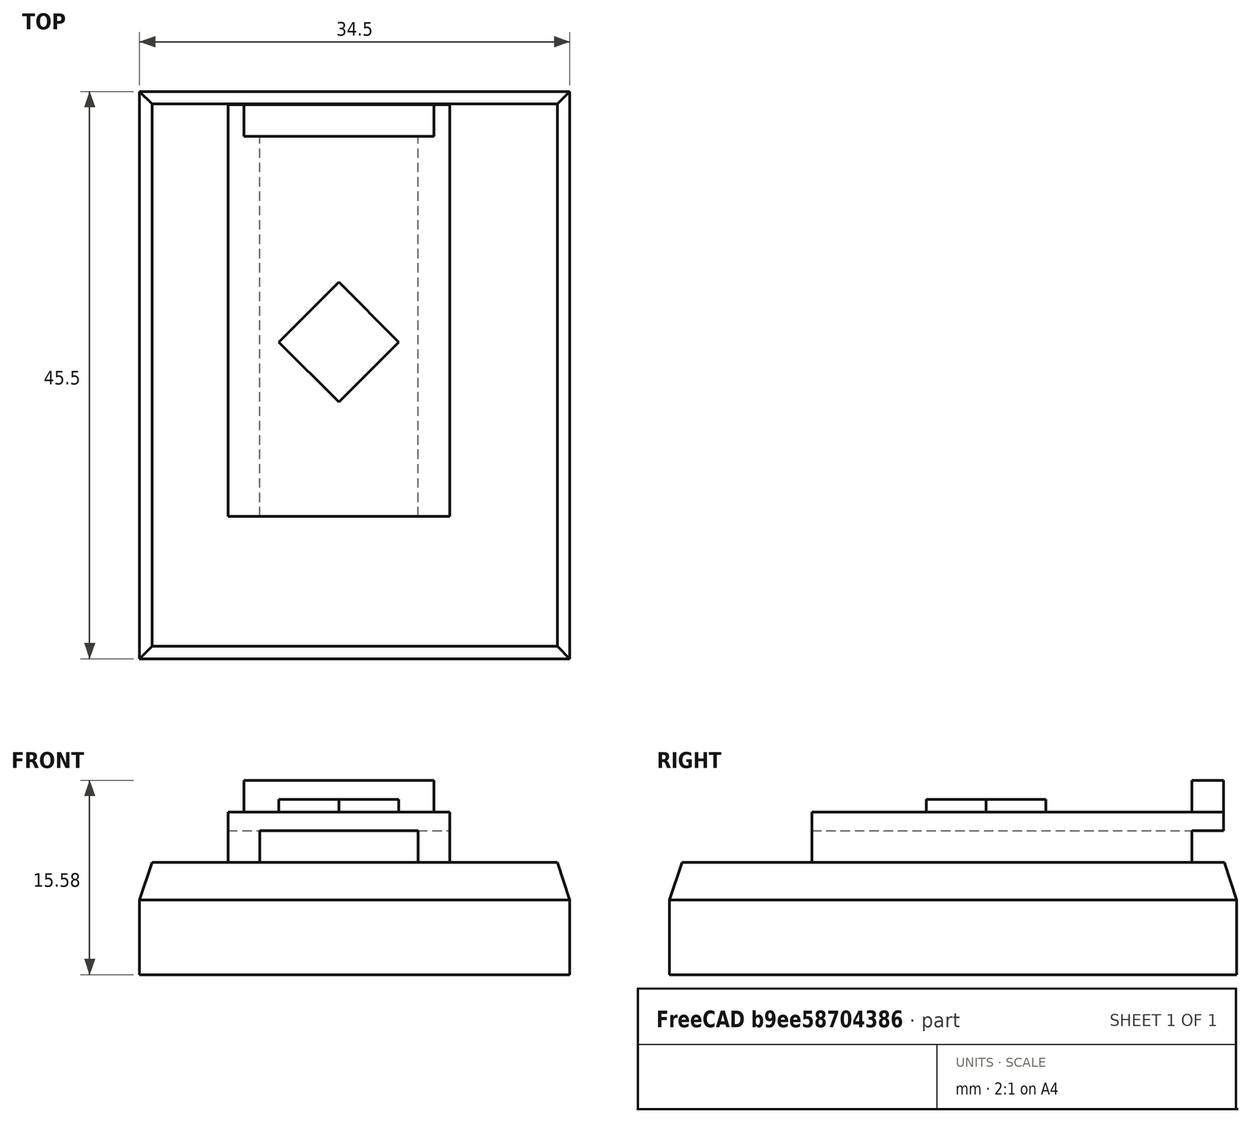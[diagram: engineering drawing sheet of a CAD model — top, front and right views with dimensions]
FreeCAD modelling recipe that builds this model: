
FCSTD DOCUMENT  (FreeCAD 0.14R3692 (Git))
Label: arduino-breadboard
License: The MIT License
LicenseURL: http://opensource.org/licenses/MIT
objects: Part::Box×5, Part::MultiFuse×2, Part::Chamfer×1, Part::Feature×1
note: 9 computed .brp shape members not serialized (recipe doc carries the construction recipe); baked Part::Feature solids carry a one-line shape summary decoded from their .brp

FEATURE [Part::Box] Box  label="breadboard"
  Height = 9
  Length = 34.5
  Width = 45.5
FEATURE [Part::Chamfer] Chamfer  label="breadboard-chamfer"
  Base = -> Box
  Edges = 4 edges: [Edge2 r1=3 r2=1,Edge6 r1=3 r2=1,Edge10 r1=3 r2=1,Edge12 r1=3 r2=1]
FEATURE [Part::Feature] Box003001  label="pin-header-left"
  Placement = pos=(15.24,0,-2.54) rot=(0,0,1;0rad)
  shape: bbox 2.54 x 30.48 x 2.54 mm, 6 faces (baked)
FEATURE [Part::Box] Box002  label="atmega-328"
  Height = 1
  Length = 6.8
  Placement = pos=(8.89,9.16167,1.5) rot=(0,0,1;0.785398rad)
  Width = 6.8
FEATURE [Part::Box] Box003  label="pin-header-right"
  Height = 2.54
  Length = 2.54
  Placement = pos=(0,0,-2.54) rot=(0,0,1;0rad)
  Width = 30.48
FEATURE [Part::Box] Box003002  label="pin-header-rear"
  Height = 2.54
  Length = 15.24
  Placement = pos=(1.27,30.48,1.5) rot=(0,0,1;0rad)
  Width = 2.54
FEATURE [Part::Box] Box001  label="pcb"
  Height = 1.5
  Length = 17.78
  Width = 33.02
FEATURE [Part::MultiFuse] Fusion  label="arduino-board"
  Placement = pos=(7.09,11.43,11.54) rot=(0,0,1;0rad)
  Shapes = -> [Box001,Box003001,Box003002,Box002,Box003]
FEATURE [Part::MultiFuse] Fusion001  label="arduino-breadboard"
  Placement = pos=(-17.25,0,0) rot=(0,0,1;0rad)
  Shapes = -> [Chamfer,Fusion]
